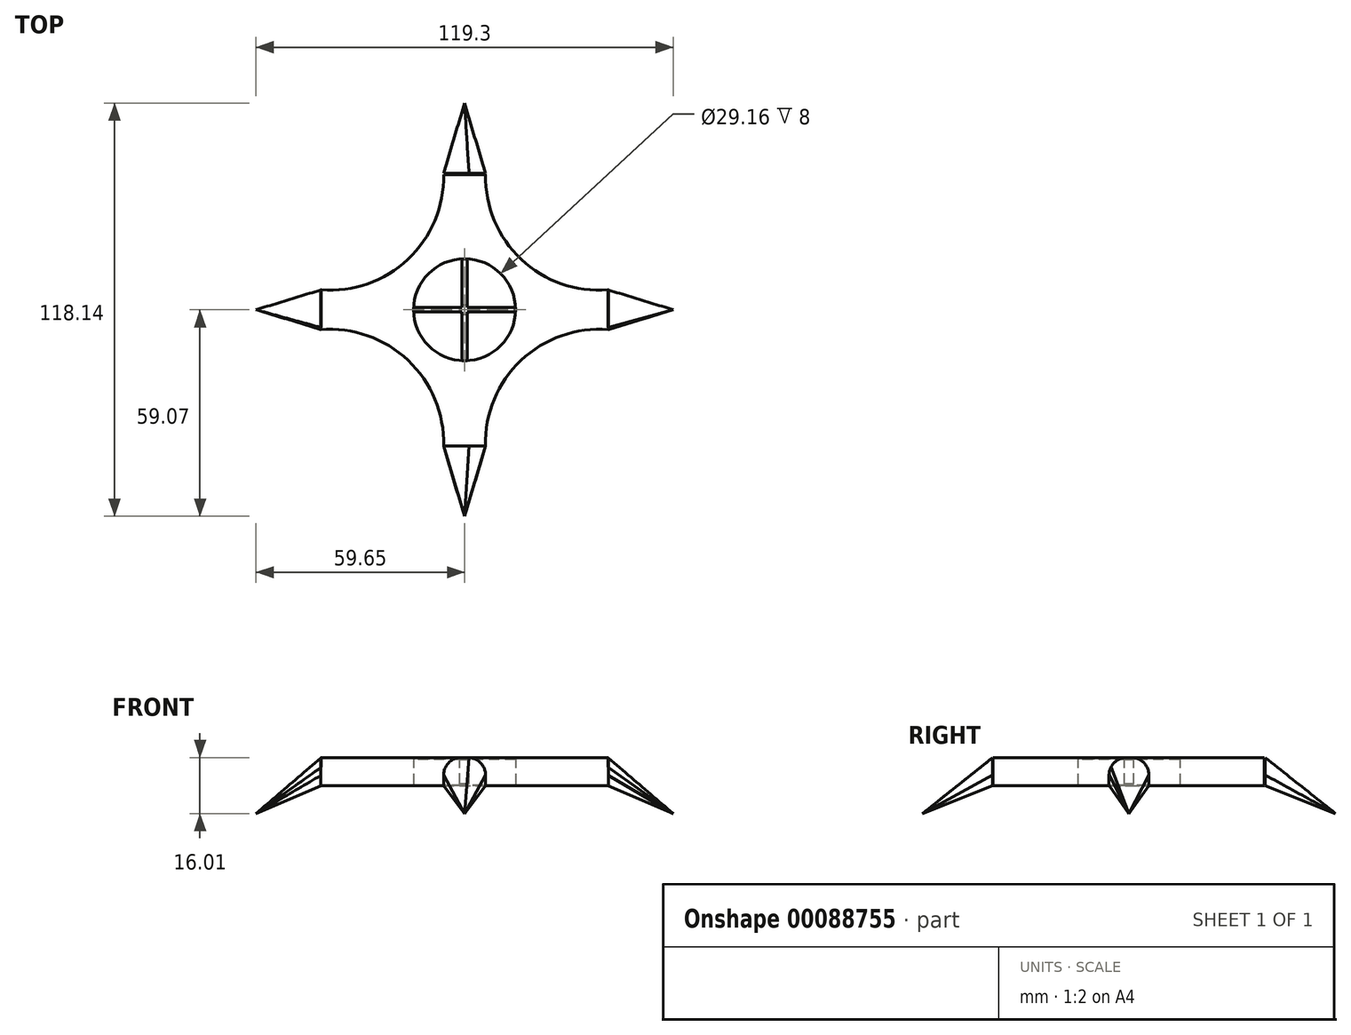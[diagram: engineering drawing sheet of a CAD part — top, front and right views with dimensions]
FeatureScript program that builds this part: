
annotation { "Feature Type Name" : "Feature", "Feature Type Description" : "" }
export const myFeature = defineFeature(function(context is Context, id is Id, definition is map)
    precondition{}
    {
        {
            var Q0;
            Q0=qCreatedBy(makeId("Top.planeOp"),FACE);
            var sketch = newSketch(context, id + "F0", { "sketchPlane" : qUnion([Q0])});
            skLineSegment(sketch, "E0", {"start": v(0, -38.93) * mm, "end": v(0, 38.65) * mm});
            skArc(sketch, "E1.MirrorCS", {"start": v(-41.16, 5.7) * mm, "mid": v(-16.26, 14.36) * mm, "end": v(-6, 38.65) * mm});
            skArc(sketch, "E2.MirrorCS", {"start": v(-41.16, -5.7) * mm, "mid": v(-16.15, -14.46) * mm, "end": v(-6, -38.93) * mm});
            skLineSegment(sketch, "E3.MirrorCS", {"start": v(-6, -38.93) * mm, "end": v(0, -38.93) * mm});
            skLineSegment(sketch, "E4.MirrorCS", {"start": v(-41.16, 5.7) * mm, "end": v(-41.16, -5.7) * mm});
            skLineSegment(sketch, "E5.MirrorCS", {"start": v(-6, 38.65) * mm, "end": v(0, 38.65) * mm});
            skPoint(sketch, "E6", {"position": v(-41.16, 0) * mm});
            skArc(sketch, "E7.MirrorCS", {"start": v(41.16, 5.7) * mm, "mid": v(16.26, 14.36) * mm, "end": v(6, 38.65) * mm});
            skArc(sketch, "E8.MirrorCS", {"start": v(41.16, -5.7) * mm, "mid": v(16.15, -14.46) * mm, "end": v(6, -38.93) * mm});
            skLineSegment(sketch, "E9.MirrorCS", {"start": v(41.16, 5.7) * mm, "end": v(41.16, -5.7) * mm});
            skLineSegment(sketch, "E10.MirrorCS", {"start": v(6, -38.93) * mm, "end": v(0, -38.93) * mm});
            skLineSegment(sketch, "E11.MirrorCS", {"start": v(6, 38.65) * mm, "end": v(0, 38.65) * mm});
            skSolve(sketch);
        }
        {
            var Q0;
            Q0 = qSketchRegion(id + "F0", true);
            extrude(context, id + "F1", {"entities" : qUnion([Q0]), "depth" : 8 * mm});
        }
        {
            var Q0;
            Q0=qCreatedBy(makeId("Right.planeOp"),FACE);
            cPlane(context, id + "F2", {"entities" : qUnion([Q0]), "cplaneType" : CPlaneType.OFFSET, "offset" : 41 * mm, "width" : 150 * mm, "height" : 150 * mm});
        }
        {
            var Q0;
            Q0=qCreatedBy(makeId("Top.planeOp"),FACE);
            cPlane(context, id + "F3", {"entities" : qUnion([Q0]), "cplaneType" : CPlaneType.OFFSET, "offset" : 8 * mm, "oppositeDirection" : true, "width" : 150 * mm, "height" : 150 * mm});
        }
        {
            var Q0;
            Q0=qCreatedBy(id+"F3.planeOp",FACE);
            var sketch = newSketch(context, id + "F4", { "sketchPlane" : qUnion([Q0])});
            skPoint(sketch, "E12", {"position": v(59.65, 0) * mm});
            skSolve(sketch);
        }
        {
            var Q0;
            Q0=makeQuery(id+"F1.opExtrude","CAP_EDGE",EDGE,{"disambiguationData":[OSD([sQuery(id+"F0.wireOp",EDGE,"6LJwIjBM-OJV4-Z8pV-JxlW-RuK7MZiSRpVA")])],"isStart":false});
            var Q1;
            Q1=makeQuery(id+"F1.opExtrude","CAP_EDGE",EDGE,{"disambiguationData":[OSD([sQuery(id+"F0.wireOp",EDGE,"E1.MirrorCS")])],"isStart":false});
            var Q2;
            Q2=makeQuery(id+"F1.opExtrude","CAP_EDGE",EDGE,{"disambiguationData":[OSD([sQuery(id+"F0.wireOp",EDGE,"E2.MirrorCS")])],"isStart":false});
            var Q3;
            Q3=makeQuery(id+"F1.opExtrude","CAP_EDGE",EDGE,{"disambiguationData":[OSD([sQuery(id+"F0.wireOp",EDGE,"WTL4JDLH-cZEB-m9iY-ICZx-Q9U5f0OPBQZo")])],"isStart":false});
            var Q4;
            Q4=makeQuery(id+"F1.opExtrude","CAP_EDGE",EDGE,{"disambiguationData":[OSD([sQuery(id+"F0.wireOp",EDGE,"E7.MirrorCS")])],"isStart":false});
            var Q5;
            Q5=makeQuery(id+"F1.opExtrude","CAP_EDGE",EDGE,{"disambiguationData":[OSD([sQuery(id+"F0.wireOp",EDGE,"E8.MirrorCS")])],"isStart":false});
            fillet(context, id + "F5", {"entities" : qUnion([Q0, Q1, Q2, Q3, Q4, Q5]), "radius" : 5 * mm, "tangentPropagation" : true, "allowEdgeOverflow" : false});
        }
        {
            var Q0;
            Q0=qCreatedBy(id+"F2.planeOp",FACE);
            var sketch = newSketch(context, id + "F6", { "sketchPlane" : qUnion([Q0])});
            skLineSegment(sketch, "E13", {"start": v(-5.67, 0) * mm, "end": v(5.68, 0) * mm});
            skLineSegment(sketch, "E14", {"start": v(5.68, 0) * mm, "end": v(5.68, 2.99) * mm});
            skLineSegment(sketch, "E15", {"start": v(-5.67, 0) * mm, "end": v(-5.67, 2.99) * mm});
            skFitSpline(sketch, "E16", {"points": [v(5.68, 2.99) * mm, v(5.68, 3.62) * mm, v(5.53, 4.17) * mm, v(5.4, 4.68) * mm, v(5.15, 5.27) * mm, v(4.86, 5.77) * mm, v(4.59, 6.14) * mm, v(4.18, 6.57) * mm, v(3.66, 7.03) * mm, v(2.9, 7.48) * mm, v(2, 7.8) * mm, v(1.34, 7.94) * mm, v(0.7, 8) * mm, v(0, 8) * mm, v(-0.7, 7.97) * mm, v(-1.4, 7.93) * mm, v(-1.98, 7.8) * mm, v(-2.82, 7.52) * mm, v(-3.45, 7.17) * mm, v(-3.88, 6.87) * mm, v(-4.23, 6.52) * mm, v(-4.52, 6.17) * mm, v(-4.82, 5.8) * mm, v(-5.11, 5.27) * mm], "startDerivative": vector(1.08, 14.84) * mm, "endDerivative": vector(-6.32, -13.3) * mm});
            skFitSpline(sketch, "E17", {"points": [v(-5.11, 5.27) * mm, v(-5.32, 4.88) * mm, v(-5.44, 4.47) * mm, v(-5.58, 4) * mm, v(-5.66, 3.42) * mm, v(-5.67, 2.99) * mm], "startDerivative": vector(-1.18, -1.99) * mm, "endDerivative": vector(0, -2.18) * mm});
            skSolve(sketch);
        }
        {
            var Q1;
            Q1=sQuery(id+"F4.wireOp",VERTEX,"E12");
            var Q2;
            Q2 = qSketchRegion(id + "F6", true);
            loft(context, id + "F7", {"sheetProfilesArray" : [{ "sheetProfileEntities" : qUnion([Q1]) }, { "sheetProfileEntities" : qUnion([Q2]) }]});
        }
        {
            var Q0;
            Q0=qCreatedBy(makeId("Front.planeOp"),FACE);
            cPlane(context, id + "F8", {"entities" : qUnion([Q0]), "cplaneType" : CPlaneType.OFFSET, "offset" : 39 * mm, "width" : 150 * mm, "height" : 150 * mm});
        }
        {
            var Q0;
            Q0=makeQuery(id+"F7.opLoft","SWEPT_BODY",BODY,{"disambiguationData":[OSD([sQuery(id+"F4.wireOp",VERTEX,"E12"),makeQuery(id+"F6.imprint","IMPRINT",FACE,{"disambiguationData":[TD([[makeQuery(id+"F6.imprint","IMPRINT",EDGE,{"derivedFrom":sQuery(id+"F6.wireOp",EDGE,"E13")}),1.0]])]})])]});
            var Q1;
            Q1=qCreatedBy(makeId("Right.planeOp"),FACE);
            mirror(context, id + "F9", {"entities" : qUnion([Q0]), "mirrorPlane" : qUnion([Q1])});
        }
        {
            var Q0;
            Q0=qCreatedBy(makeId("Top.planeOp"),FACE);
            var sketch = newSketch(context, id + "F10", { "sketchPlane" : qUnion([Q0])});
            skCircle(sketch, "E18", {"center": v(0, 0) * mm, "radius": 14.58 * mm});
            skSolve(sketch);
        }
        {
            var Q0;
            Q0 = qSketchRegion(id + "F10", true);
            extrude(context, id + "F11", {"entities" : qUnion([Q0]), "operationType" : NewBodyOperationType.REMOVE, "depth" : 25 * mm, "hasSecondDirection" : true, "secondDirectionOppositeDirection" : true, "secondDirectionDepth" : 25 * mm});
        }
        {
            var Q0;
            Q0=qCreatedBy(makeId("Top.planeOp"),FACE);
            cPlane(context, id + "F12", {"entities" : qUnion([Q0]), "cplaneType" : CPlaneType.OFFSET, "offset" : 7.5 * mm, "width" : 150 * mm, "height" : 150 * mm});
        }
        {
            var Q0;
            Q0=qCreatedBy(id+"F8.planeOp",FACE);
            var sketch = newSketch(context, id + "F13", { "sketchPlane" : qUnion([Q0])});
            skLineSegment(sketch, "E19", {"start": v(-6, 0) * mm, "end": v(6, 0) * mm});
            skLineSegment(sketch, "E20", {"start": v(6, 0) * mm, "end": v(6, 3) * mm});
            skLineSegment(sketch, "E21", {"start": v(-6, 0) * mm, "end": v(-6, 3) * mm});
            skFitSpline(sketch, "E22", {"points": [v(-6, 3) * mm, v(-6, 3.16) * mm, v(-5.98, 3.38) * mm, v(-5.97, 3.53) * mm, v(-5.95, 3.73) * mm, v(-5.9, 3.94) * mm, v(-5.87, 4.1) * mm, v(-5.8, 4.37) * mm, v(-5.74, 4.57) * mm, v(-5.6, 4.94) * mm, v(-5.49, 5.2) * mm, v(-5.45, 5.27) * mm, v(-5.36, 5.44) * mm, v(-5.3, 5.55) * mm, v(-5.22, 5.68) * mm, v(-5.05, 5.92) * mm, v(-4.96, 6.06) * mm, v(-4.87, 6.15) * mm, v(-4.78, 6.26) * mm, v(-4.71, 6.35) * mm, v(-4.5, 6.56) * mm, v(-4.3, 6.76) * mm, v(-4.16, 6.87) * mm, v(-3.95, 7.03) * mm, v(-3.74, 7.18) * mm, v(-3.63, 7.25) * mm, v(-3.4, 7.38) * mm, v(-3.28, 7.44) * mm, v(-3.17, 7.5) * mm, v(-3.03, 7.57) * mm, v(-2.92, 7.61) * mm, v(-2.59, 7.74) * mm, v(-2.32, 7.82) * mm, v(-1.88, 7.92) * mm, v(-1.65, 7.95) * mm, v(-1.34, 7.99) * mm, v(-1.02, 8) * mm, v(1.27, 8) * mm], "startDerivative": vector(-0.08, 6.91) * mm, "endDerivative": vector(33.76, -0.13) * mm});
            skFitSpline(sketch, "E23", {"points": [v(1.27, 8) * mm, v(1.94, 7.9) * mm, v(2.89, 7.63) * mm, v(3.5, 7.34) * mm, v(4.14, 6.87) * mm, v(4.62, 6.45) * mm, v(5.1, 5.84) * mm, v(5.47, 5.24) * mm, v(5.67, 4.8) * mm, v(5.88, 4.11) * mm, v(5.98, 3.47) * mm, v(6, 3) * mm], "startDerivative": vector(6.91, -0.67) * mm, "endDerivative": vector(-0.06, -6.05) * mm});
            skSolve(sketch);
        }
        {
            var Q0;
            Q0=qCreatedBy(id+"F3.planeOp",FACE);
            var sketch = newSketch(context, id + "F14", { "sketchPlane" : qUnion([Q0])});
            skPoint(sketch, "E24", {"position": v(0, -59.07) * mm});
            skSolve(sketch);
        }
        {
            var Q0;
            Q0=sQuery(id+"F14.wireOp",VERTEX,"E24");
            var Q1;
            Q1 = qSketchRegion(id + "F13", true);
            loft(context, id + "F15", {"sheetProfilesArray" : [{ "sheetProfileEntities" : qUnion([Q0]) }, { "sheetProfileEntities" : qUnion([Q1]) }]});
        }
        {
            var Q0;
            Q0=makeQuery(id+"F15.opLoft","SWEPT_BODY",BODY,{"disambiguationData":[OSD([makeQuery(id+"F13.imprint","IMPRINT",FACE,{"disambiguationData":[TD([[makeQuery(id+"F13.imprint","IMPRINT",EDGE,{"derivedFrom":sQuery(id+"F13.wireOp",EDGE,"E19")}),1.0]])]}),sQuery(id+"F14.wireOp",VERTEX,"E24")])]});
            var Q1;
            Q1=qCreatedBy(makeId("Front.planeOp"),FACE);
            mirror(context, id + "F16", {"entities" : qUnion([Q0]), "mirrorPlane" : qUnion([Q1])});
        }
        {
            var Q0;
            Q0=qCreatedBy(id+"F12.planeOp",FACE);
            var sketch = newSketch(context, id + "F17", { "sketchPlane" : qUnion([Q0])});
            skCircle(sketch, "E25", {"center": v(0, 0) * mm, "radius": 1.34 * mm});
            skSolve(sketch);
        }
        {
            var Q0;
            Q0=makeQuery(id+"F17.imprint","IMPRINT",FACE,{"disambiguationData":[TD([[makeQuery(id+"F17.imprint","IMPRINT",EDGE,{"derivedFrom":sQuery(id+"F17.wireOp",EDGE,"E25")}),1.0]])]});
            extrude(context, id + "F18", {"entities" : qUnion([Q0]), "oppositeDirection" : true, "depth" : 7 * mm});
        }
        {
            var Q0;
            Q0=qCreatedBy(id+"F12.planeOp",FACE);
            var sketch = newSketch(context, id + "F19", { "sketchPlane" : qUnion([Q0])});
            skLineSegment(sketch, "E26.bottom", {"start": v(14.53, 0.64) * mm, "end": v(-14.53, 0.64) * mm});
            skLineSegment(sketch, "E26.top", {"start": v(14.53, -0.64) * mm, "end": v(-14.53, -0.64) * mm});
            skLineSegment(sketch, "E26.left", {"start": v(14.53, 0.64) * mm, "end": v(14.53, -0.64) * mm});
            skLineSegment(sketch, "E26.right", {"start": v(-14.53, 0.64) * mm, "end": v(-14.53, -0.64) * mm});
            skPoint(sketch, "E26.middle", {"position": v(0, 0) * mm});
            skLineSegment(sketch, "E27.bottom", {"start": v(-0.74, 14.52) * mm, "end": v(0.74, 14.52) * mm});
            skLineSegment(sketch, "E27.top", {"start": v(-0.74, -14.52) * mm, "end": v(0.74, -14.52) * mm});
            skLineSegment(sketch, "E27.left", {"start": v(-0.74, 14.52) * mm, "end": v(-0.74, -14.52) * mm});
            skLineSegment(sketch, "E27.right", {"start": v(0.74, 14.52) * mm, "end": v(0.74, -14.52) * mm});
            skSolve(sketch);
        }
        {
            var Q0;
            Q0 = qSketchRegion(id + "F19", true);
            extrude(context, id + "F20", {"entities" : qUnion([Q0]), "operationType" : NewBodyOperationType.ADD, "depth" : 0.1 * mm});
        }
        {
            var Q0;
            Q0=qCreatedBy(makeId("Top.planeOp"),FACE);
            var sketch = newSketch(context, id + "F21", { "sketchPlane" : qUnion([Q0])});
            skLineSegment(sketch, "E28.bottom", {"start": v(14.53, 0.62) * mm, "end": v(-14.53, 0.62) * mm});
            skLineSegment(sketch, "E28.top", {"start": v(14.53, -0.66) * mm, "end": v(-14.53, -0.66) * mm});
            skLineSegment(sketch, "E28.left", {"start": v(14.53, 0.62) * mm, "end": v(14.53, -0.66) * mm});
            skLineSegment(sketch, "E28.right", {"start": v(-14.53, 0.62) * mm, "end": v(-14.53, -0.66) * mm});
            skPoint(sketch, "E28.middle", {"position": v(0, -0.02) * mm});
            skLineSegment(sketch, "E29.bottom", {"start": v(-0.74, 14.5) * mm, "end": v(0.74, 14.5) * mm});
            skLineSegment(sketch, "E29.top", {"start": v(-0.74, -14.54) * mm, "end": v(0.74, -14.54) * mm});
            skLineSegment(sketch, "E29.left", {"start": v(-0.74, 14.5) * mm, "end": v(-0.74, -14.54) * mm});
            skLineSegment(sketch, "E29.right", {"start": v(0.74, 14.5) * mm, "end": v(0.74, -14.54) * mm});
            skSolve(sketch);
        }
        {
            var Q0;
            Q0 = qSketchRegion(id + "F21", true);
            extrude(context, id + "F22", {"entities" : qUnion([Q0]), "depth" : 0.1 * mm});
        }
    });
